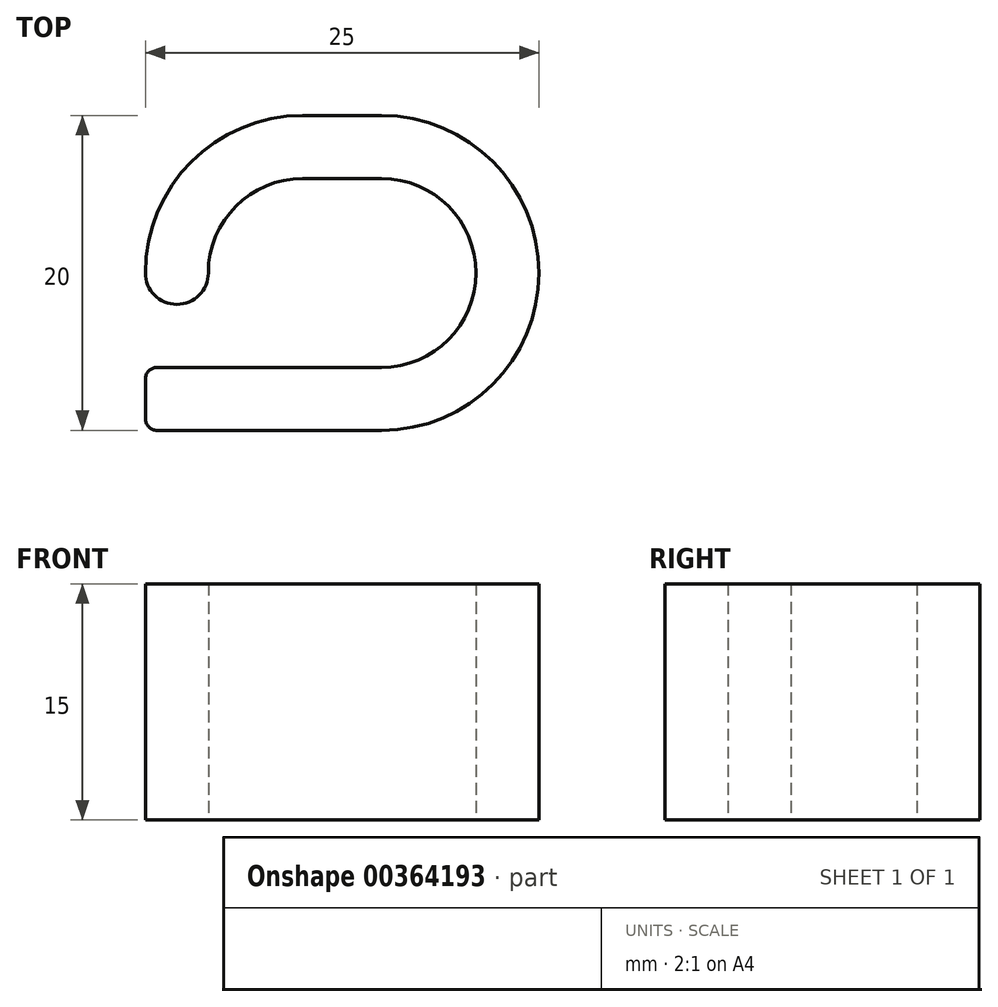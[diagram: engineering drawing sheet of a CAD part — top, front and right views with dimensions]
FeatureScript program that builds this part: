
annotation { "Feature Type Name" : "Feature", "Feature Type Description" : "" }
export const myFeature = defineFeature(function(context is Context, id is Id, definition is map)
    precondition{}
    {
        {
            var Q0;
            Q0=qCreatedBy(makeId("Top.planeOp"),FACE);
            var sketch = newSketch(context, id + "F0", { "sketchPlane" : qUnion([Q0])});
            skArc(sketch, "E0", {"start": v(0, -6) * mm, "mid": v(4.24, -4.24) * mm, "end": v(6, 0) * mm});
            skLineSegment(sketch, "E1", {"start": v(0, -6) * mm, "end": v(-14.25, -6) * mm});
            skArc(sketch, "E2", {"start": v(0, -10) * mm, "mid": v(7.07, -7.07) * mm, "end": v(10, 0) * mm});
            skLineSegment(sketch, "E3", {"start": v(0, -10) * mm, "end": v(-14.25, -10) * mm});
            skLineSegment(sketch, "E4", {"start": v(0, 0) * mm, "end": v(0, 6) * mm, "construction": true});
            skArc(sketch, "E5", {"start": v(-5, 10) * mm, "mid": v(-12.07, 7.07) * mm, "end": v(-15, 0) * mm});
            skLineSegment(sketch, "E6", {"start": v(0, 6) * mm, "end": v(0, 6) * mm});
            skArc(sketch, "E7", {"start": v(-5, 6) * mm, "mid": v(-9.24, 4.24) * mm, "end": v(-11, 0) * mm});
            skLineSegment(sketch, "E8", {"start": v(0, 10) * mm, "end": v(-5, 10) * mm});
            skLineSegment(sketch, "E9", {"start": v(0, 6) * mm, "end": v(-5, 6) * mm});
            skLineSegment(sketch, "E10", {"start": v(-15, -6.75) * mm, "end": v(-15, -9.25) * mm});
            skPoint(sketch, "E11.visualSharp", {"position": v(-15, -6) * mm});
            skArc(sketch, "E11.filletArc", {"start": v(-14.25, -6) * mm, "mid": v(-14.78, -6.22) * mm, "end": v(-15, -6.75) * mm});
            skPoint(sketch, "E12.visualSharp", {"position": v(-15, -10) * mm});
            skArc(sketch, "E12.filletArc", {"start": v(-15, -9.25) * mm, "mid": v(-14.78, -9.78) * mm, "end": v(-14.25, -10) * mm});
            skArc(sketch, "E13", {"start": v(-15, 0) * mm, "mid": v(-13, -2) * mm, "end": v(-11, 0) * mm});
            skLineSegment(sketch, "E14", {"start": v(0, 0) * mm, "end": v(6, 0) * mm, "construction": true});
            skLineSegment(sketch, "E15", {"start": v(6, 0) * mm, "end": v(10, 0) * mm, "construction": true});
            skArc(sketch, "E16", {"start": v(6, 0) * mm, "mid": v(4.24, 4.24) * mm, "end": v(0, 6) * mm});
            skLineSegment(sketch, "E17", {"start": v(10, 0) * mm, "end": v(10, 0) * mm});
            skArc(sketch, "E18", {"start": v(10, 0) * mm, "mid": v(7.07, 7.07) * mm, "end": v(0, 10) * mm});
            skSolve(sketch);
        }
        {
            var Q0;
            Q0=qSketchRegion(id+"F0",true);
            extrude(context, id + "F1", {"entities" : qUnion([Q0]), "depth" : 15 * mm});
        }
    });
